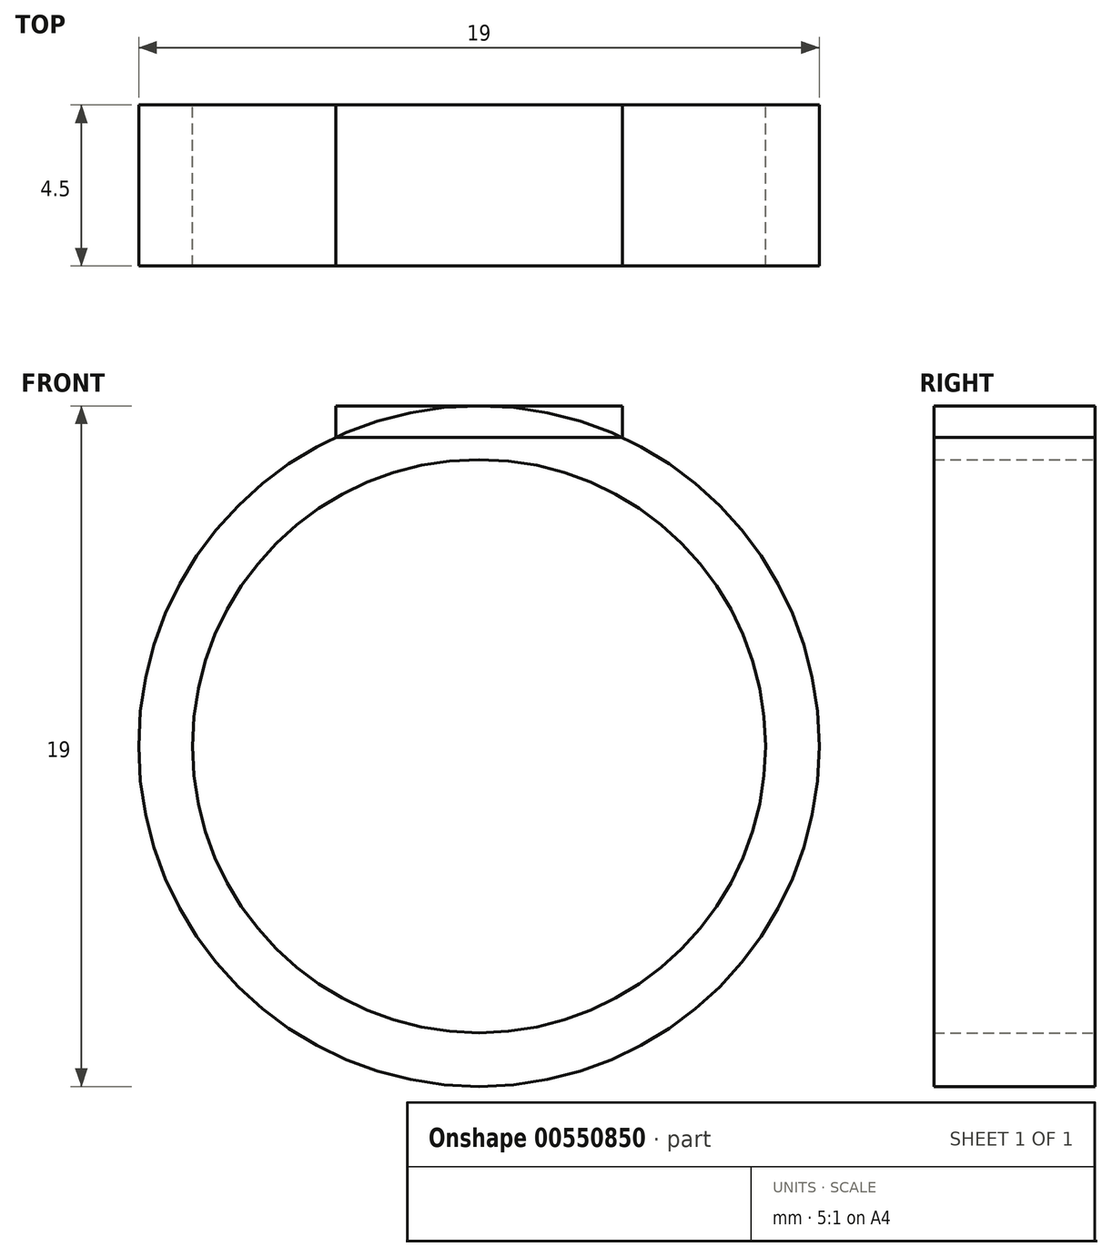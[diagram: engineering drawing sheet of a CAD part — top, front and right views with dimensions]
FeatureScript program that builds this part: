
annotation { "Feature Type Name" : "Feature", "Feature Type Description" : "" }
export const myFeature = defineFeature(function(context is Context, id is Id, definition is map)
    precondition{}
    {
        {
            var Q0;
            Q0=qCreatedBy(makeId("Front.planeOp"),FACE);
            var sketch = newSketch(context, id + "F0", { "sketchPlane" : qUnion([Q0])});
            skCircle(sketch, "E0", {"center": v(0, 0) * mm, "radius": 8 * mm});
            skCircle(sketch, "E1", {"center": v(0, 0) * mm, "radius": 9.5 * mm});
            skSolve(sketch);
        }
        {
            var Q0;
            Q0=makeQuery(id+"F0.imprint","IMPRINT",FACE,{"disambiguationData":[TD([[makeQuery(id+"F0.imprint","IMPRINT",EDGE,{"derivedFrom":sQuery(id+"F0.wireOp",EDGE,"E0")}),-1.0]])]});
            extrude(context, id + "F1", {"entities" : qUnion([Q0]), "depth" : 4.5 * mm, "offsetDistance" : 25 * mm});
        }
        {
            var Q0;
            Q0=qCreatedBy(makeId("Front.planeOp"),FACE);
            var sketch = newSketch(context, id + "F2", { "sketchPlane" : qUnion([Q0])});
            skLineSegment(sketch, "E2", {"start": v(-4, 9.5) * mm, "end": v(4, 9.5) * mm});
            skLineSegment(sketch, "E3", {"start": v(4, 9.5) * mm, "end": v(4, 8.62) * mm});
            skLineSegment(sketch, "E4", {"start": v(-4, 9.5) * mm, "end": v(-4, 8.62) * mm});
            skLineSegment(sketch, "E5", {"start": v(-4, 8.62) * mm, "end": v(4, 8.62) * mm});
            skSolve(sketch);
        }
        {
            var Q0;
            Q0 = qSketchRegion(id + "F2", true);
            extrude(context, id + "F3", {"entities" : qUnion([Q0]), "depth" : 4.5 * mm, "offsetDistance" : 25 * mm});
        }
    });
